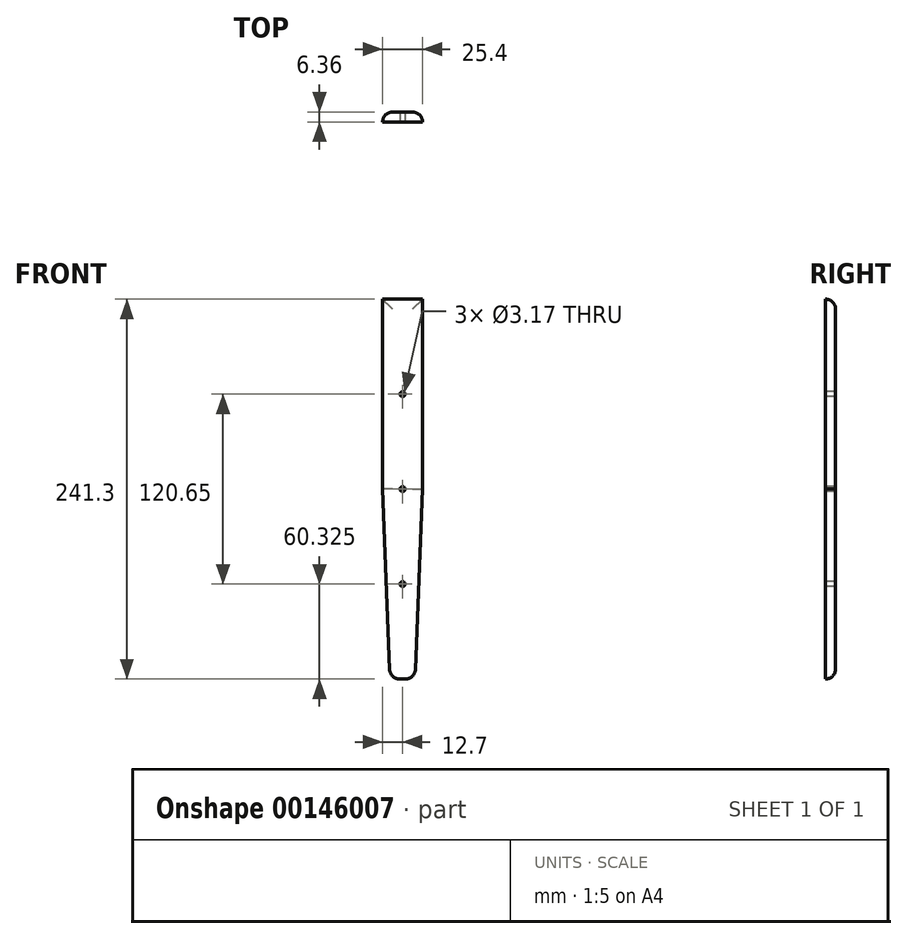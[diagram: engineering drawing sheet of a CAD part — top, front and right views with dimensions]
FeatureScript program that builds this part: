
annotation { "Feature Type Name" : "Feature", "Feature Type Description" : "" }
export const myFeature = defineFeature(function(context is Context, id is Id, definition is map)
    precondition{}
    {
        {
            var Q0;
            Q0=qCreatedBy(makeId("Front.planeOp"),FACE);
            cPlane(context, id + "F0", {"entities" : qUnion([Q0]), "cplaneType" : CPlaneType.OFFSET, "offset" : 3.17 * mm, "oppositeDirection" : true, "width" : 152.4 * mm, "height" : 152.4 * mm});
        }
        {
            var Q0;
            Q0=qCreatedBy(id+"F0.planeOp",FACE);
            var sketch = newSketch(context, id + "F1", { "sketchPlane" : qUnion([Q0])});
            skLineSegment(sketch, "E0", {"start": v(0, 0) * mm, "end": v(0, -304.8) * mm, "construction": true});
            skPoint(sketch, "E1", {"position": v(0, -254) * mm});
            skPoint(sketch, "E2", {"position": v(0, -12.7) * mm});
            skPoint(sketch, "E3", {"position": v(0, -133.35) * mm});
            skPoint(sketch, "E4", {"position": v(0, -73.02) * mm});
            skPoint(sketch, "E5", {"position": v(0, -193.67) * mm});
            skLineSegment(sketch, "E6", {"start": v(12.7, -133.35) * mm, "end": v(-12.7, -133.35) * mm, "construction": true});
            skLineSegment(sketch, "E7", {"start": v(12.7, -12.7) * mm, "end": v(-12.7, -12.7) * mm});
            skLineSegment(sketch, "E8", {"start": v(7.94, -254) * mm, "end": v(-7.94, -254) * mm});
            skLineSegment(sketch, "E9", {"start": v(12.7, -12.7) * mm, "end": v(12.7, -133.35) * mm});
            skLineSegment(sketch, "E10", {"start": v(12.7, -133.35) * mm, "end": v(7.94, -254) * mm});
            skLineSegment(sketch, "E11", {"start": v(-12.7, -12.7) * mm, "end": v(-12.7, -133.35) * mm});
            skLineSegment(sketch, "E12", {"start": v(-12.7, -133.35) * mm, "end": v(-7.94, -254) * mm});
            skSolve(sketch);
        }
        {
            var Q0;
            Q0=makeQuery(id+"F1.imprint","IMPRINT",FACE,{"disambiguationData":[TD([[makeQuery(id+"F1.imprint","IMPRINT",EDGE,{"derivedFrom":sQuery(id+"F1.wireOp",EDGE,"E7")}),1.0]])]});
            extrude(context, id + "F2", {"entities" : qUnion([Q0]), "oppositeDirection" : true, "depth" : 6.35 * mm});
        }
        {
            var Q0;
            Q0=sQuery(id+"F1.wireOp",VERTEX,"E4");
            var Q1;
            Q1=sQuery(id+"F1.wireOp",VERTEX,"E3");
            var Q2;
            Q2=sQuery(id+"F1.wireOp",VERTEX,"E5");
            var Q3;
            Q3=makeQuery(id+"F2.opExtrude","SWEPT_BODY",BODY,{"disambiguationData":[OSD([sQuery(id+"F1.wireOp",EDGE,"E7"),sQuery(id+"F1.wireOp",EDGE,"E8"),sQuery(id+"F1.wireOp",EDGE,"E9"),sQuery(id+"F1.wireOp",EDGE,"E10"),sQuery(id+"F1.wireOp",EDGE,"E11"),sQuery(id+"F1.wireOp",EDGE,"E12")])]});
            hole(context, id + "F3", {"style" : HoleStyle.SIMPLE, "endStyle" : HoleEndStyle.THROUGH, "holeDiameter" : 3.17 * mm, "locations" : qUnion([Q0, Q1, Q2]), "scope" : qUnion([Q3]), "isTappedThrough" : true});
        }
        {
            var Q0;
            Q0=makeQuery(id+"F2.opExtrude","SWEPT_EDGE",EDGE,{"disambiguationData":[OSD([sQuery(id+"F1.wireOp",EDGE,"E8"),sQuery(id+"F1.wireOp",EDGE,"E12")])]});
            var Q1;
            Q1=makeQuery(id+"F2.opExtrude","SWEPT_EDGE",EDGE,{"disambiguationData":[OSD([sQuery(id+"F1.wireOp",EDGE,"E8"),sQuery(id+"F1.wireOp",EDGE,"E10")])]});
            fillet(context, id + "F4", {"entities" : qUnion([Q0, Q1]), "radius" : 6.35 * mm, "tangentPropagation" : true, "allowEdgeOverflow" : false});
        }
        {
            var Q0;
            Q0=makeQuery(id+"F2.opExtrude","CAP_EDGE",EDGE,{"disambiguationData":[OSD([sQuery(id+"F1.wireOp",EDGE,"E8")])],"isStart":false});
            var Q1;
            {var subQ0=sQuery(id+"F1.wireOp",EDGE,"E12");var subQ1=sQuery(id+"F1.wireOp",EDGE,"E8");Q1=makeQuery(id+"F4.opFillet","BLEND_EDGE",EDGE,{"blendedFrom":[makeQuery(id+"F2.opExtrude","SWEPT_EDGE",EDGE,{"disambiguationData":[OSD([subQ1,subQ0])]}),makeQuery(id+"F2.opExtrude","CAP_FACE",FACE,{"disambiguationData":[OSD([sQuery(id+"F1.wireOp",EDGE,"E7"),subQ1,sQuery(id+"F1.wireOp",EDGE,"E9"),sQuery(id+"F1.wireOp",EDGE,"E10"),sQuery(id+"F1.wireOp",EDGE,"E11"),subQ0])],"isStart":false})],"blendedInto":[makeQuery(id+"F2.opExtrude","CAP_FACE",FACE,{"disambiguationData":[OSD([sQuery(id+"F1.wireOp",EDGE,"E7"),subQ1,sQuery(id+"F1.wireOp",EDGE,"E9"),sQuery(id+"F1.wireOp",EDGE,"E10"),sQuery(id+"F1.wireOp",EDGE,"E11"),subQ0])],"isStart":false})]});}
            var Q2;
            {var subQ0=sQuery(id+"F1.wireOp",EDGE,"E10");var subQ1=sQuery(id+"F1.wireOp",EDGE,"E8");Q2=makeQuery(id+"F4.opFillet","BLEND_EDGE",EDGE,{"blendedFrom":[makeQuery(id+"F2.opExtrude","SWEPT_EDGE",EDGE,{"disambiguationData":[OSD([subQ1,subQ0])]}),makeQuery(id+"F2.opExtrude","CAP_FACE",FACE,{"disambiguationData":[OSD([sQuery(id+"F1.wireOp",EDGE,"E7"),subQ1,sQuery(id+"F1.wireOp",EDGE,"E9"),subQ0,sQuery(id+"F1.wireOp",EDGE,"E11"),sQuery(id+"F1.wireOp",EDGE,"E12")])],"isStart":false})],"blendedInto":[makeQuery(id+"F2.opExtrude","CAP_FACE",FACE,{"disambiguationData":[OSD([sQuery(id+"F1.wireOp",EDGE,"E7"),subQ1,sQuery(id+"F1.wireOp",EDGE,"E9"),subQ0,sQuery(id+"F1.wireOp",EDGE,"E11"),sQuery(id+"F1.wireOp",EDGE,"E12")])],"isStart":false})]});}
            var Q3;
            Q3=makeQuery(id+"F2.opExtrude","CAP_EDGE",EDGE,{"disambiguationData":[OSD([sQuery(id+"F1.wireOp",EDGE,"E10")])],"isStart":false});
            var Q4;
            Q4=makeQuery(id+"F2.opExtrude","CAP_EDGE",EDGE,{"disambiguationData":[OSD([sQuery(id+"F1.wireOp",EDGE,"E12")])],"isStart":false});
            var Q5;
            Q5=makeQuery(id+"F2.opExtrude","CAP_EDGE",EDGE,{"disambiguationData":[OSD([sQuery(id+"F1.wireOp",EDGE,"E9")])],"isStart":false});
            var Q6;
            Q6=makeQuery(id+"F2.opExtrude","CAP_EDGE",EDGE,{"disambiguationData":[OSD([sQuery(id+"F1.wireOp",EDGE,"E11")])],"isStart":false});
            var Q7;
            Q7=makeQuery(id+"F2.opExtrude","CAP_EDGE",EDGE,{"disambiguationData":[OSD([sQuery(id+"F1.wireOp",EDGE,"E7")])],"isStart":false});
            fillet(context, id + "F5", {"entities" : qUnion([Q0, Q1, Q2, Q3, Q4, Q5, Q6, Q7]), "radius" : 6.35 * mm, "tangentPropagation" : true, "allowEdgeOverflow" : false});
        }
    });
